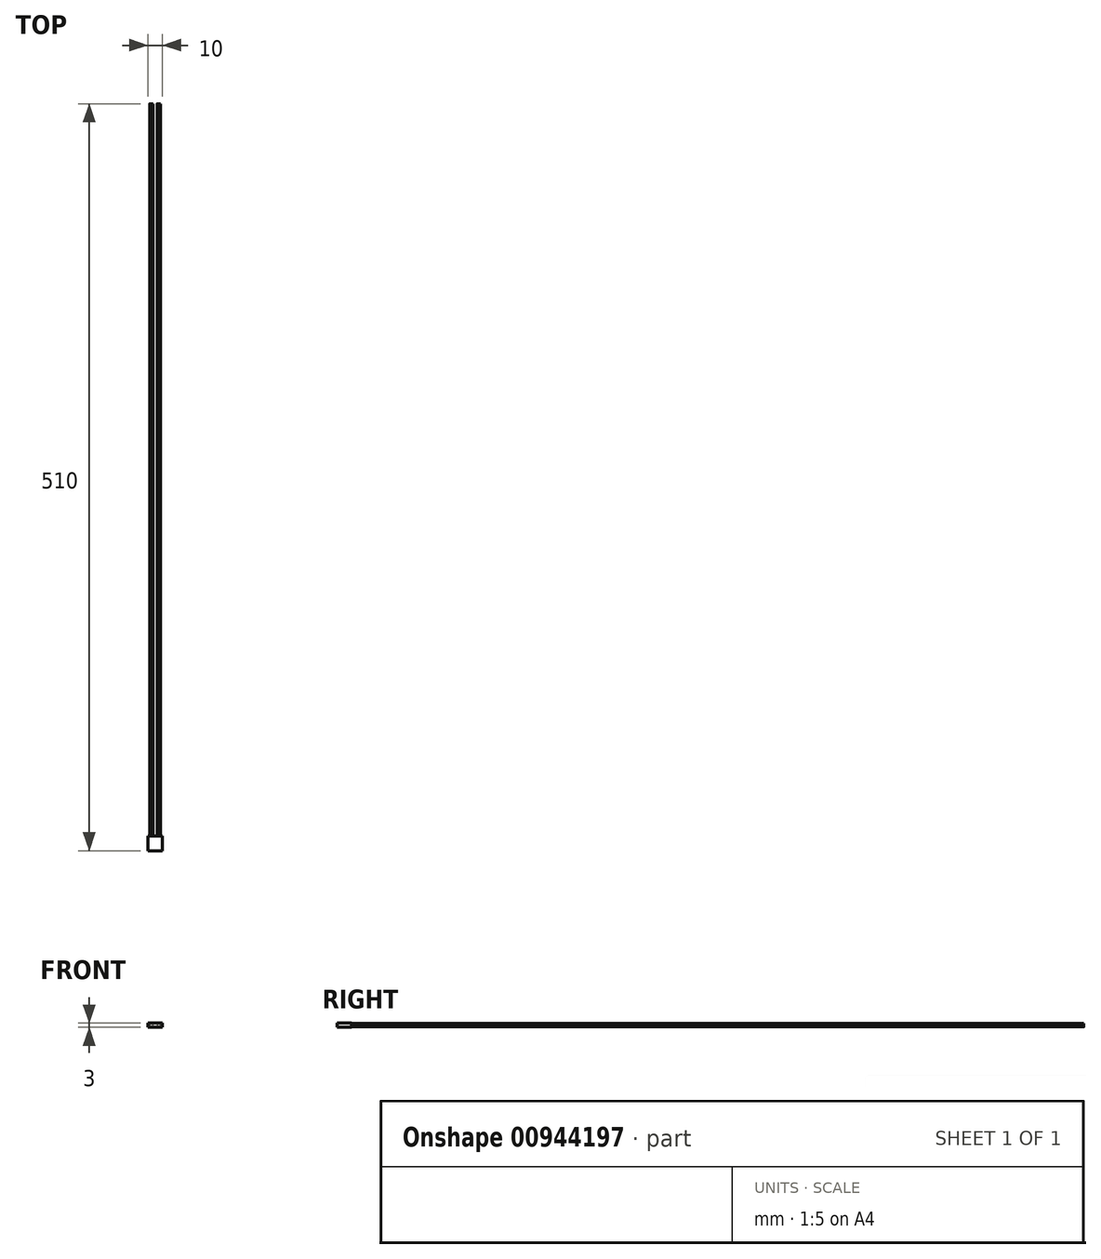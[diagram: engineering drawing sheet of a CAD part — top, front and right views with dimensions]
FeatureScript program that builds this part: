
annotation { "Feature Type Name" : "Feature", "Feature Type Description" : "" }
export const myFeature = defineFeature(function(context is Context, id is Id, definition is map)
    precondition{}
    {
        {
            var Q0;
            Q0=qCreatedBy(makeId("Top.planeOp"),FACE);
            var sketch = newSketch(context, id + "F0", { "sketchPlane" : qUnion([Q0])});
            skLineSegment(sketch, "E0.bottom", {"start": v(-5, 5.06) * mm, "end": v(5, 5.06) * mm});
            skLineSegment(sketch, "E0.top", {"start": v(-5, -4.94) * mm, "end": v(5, -4.94) * mm});
            skLineSegment(sketch, "E0.left", {"start": v(-5, 5.06) * mm, "end": v(-5, -4.94) * mm});
            skLineSegment(sketch, "E0.right", {"start": v(5, 5.06) * mm, "end": v(5, -4.94) * mm});
            skSolve(sketch);
        }
        {
            var Q0;
            Q0=makeQuery(id+"F0.imprint","IMPRINT",FACE,{"disambiguationData":[TD([[makeQuery(id+"F0.imprint","IMPRINT",EDGE,{"derivedFrom":sQuery(id+"F0.wireOp",EDGE,"E0.bottom")}),-1.0]])]});
            extrude(context, id + "F1", {"entities" : qUnion([Q0]), "depth" : 3 * mm, "offsetDistance" : 25 * mm});
        }
        {
            var Q0;
            Q0=makeQuery(id+"F1.opExtrude","SWEPT_FACE",FACE,{"disambiguationData":[OSD([sQuery(id+"F0.wireOp",EDGE,"E0.bottom")])]});
            var sketch = newSketch(context, id + "F2", { "sketchPlane" : qUnion([Q0])});
            skCircle(sketch, "E1", {"center": v(-2.5, 1.5) * mm, "radius": 1.19 * mm});
            skCircle(sketch, "E2", {"center": v(2.5, 1.5) * mm, "radius": 1.22 * mm});
            skSolve(sketch);
        }
        {
            var Q0;
            Q0=makeQuery(id+"F2.imprint","IMPRINT",FACE,{"disambiguationData":[TD([[makeQuery(id+"F2.imprint","IMPRINT",EDGE,{"derivedFrom":sQuery(id+"F2.wireOp",EDGE,"E1")}),1.0]])]});
            var Q1;
            Q1=makeQuery(id+"F2.imprint","IMPRINT",FACE,{"disambiguationData":[TD([[makeQuery(id+"F2.imprint","IMPRINT",EDGE,{"derivedFrom":sQuery(id+"F2.wireOp",EDGE,"E2")}),1.0]])]});
            extrude(context, id + "F3", {"entities" : qUnion([Q0, Q1]), "operationType" : NewBodyOperationType.ADD, "depth" : 500 * mm, "offsetDistance" : 25 * mm});
        }
    });
